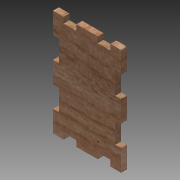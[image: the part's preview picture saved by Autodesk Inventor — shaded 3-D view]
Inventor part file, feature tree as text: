
AUTODESK INVENTOR PART (.ipt)
format: ipt  version: 2015 (Build 190159000, 159)  size: 242,688 bytes
history: native  units: mm
features: other x9, sketch x6, extrude x3
ambient origin geometry x8: Origin, YZ Plane, XZ Plane, XY Plane, X Axis, Y Axis, Z Axis, Center Point
bodies: Solid1 (feature_tree)
feature tree (18):
  other  "Blocks"
  extrude  "Extrusion1"  Depth=100.0mm
  extrude  "Extrusion3"  TaperAngle=0.0deg  [1 undecoded]
  extrude  "Extrusion4"  Depth=20.0mm
  sketch  "Sketch15"  dims[d15=5.5mm]
  sketch  "Sketch16"  dims[d16=0.0mm d17=5.5mm d18=12.0mm d19=20.0mm d20=5.5mm d21=0.0mm]
  sketch  "Sketch14"  dims[d14=5.5mm]
  sketch  "Sketch1"  dims[d0=64.0mm d1=100.0mm]
  sketch  "Sketch5"  dims[d2=5.5mm d3=0.0mm]
  sketch  "Sketch6"  dims[d12=20.0mm d13=20.0mm]
  other  "Block1"
  other  "Block2"
  other  "Block3"
  other  "Block4"
  other  "Block3:1"
  other  "Block3:2"
  other  "Block4:1"
  other  "Block4:2"
note: 1 required parameter value undecoded (feature->parameter linkage not recoverable at this tier; creation-order binding heuristic only, values carry confidence <= 0.55)
